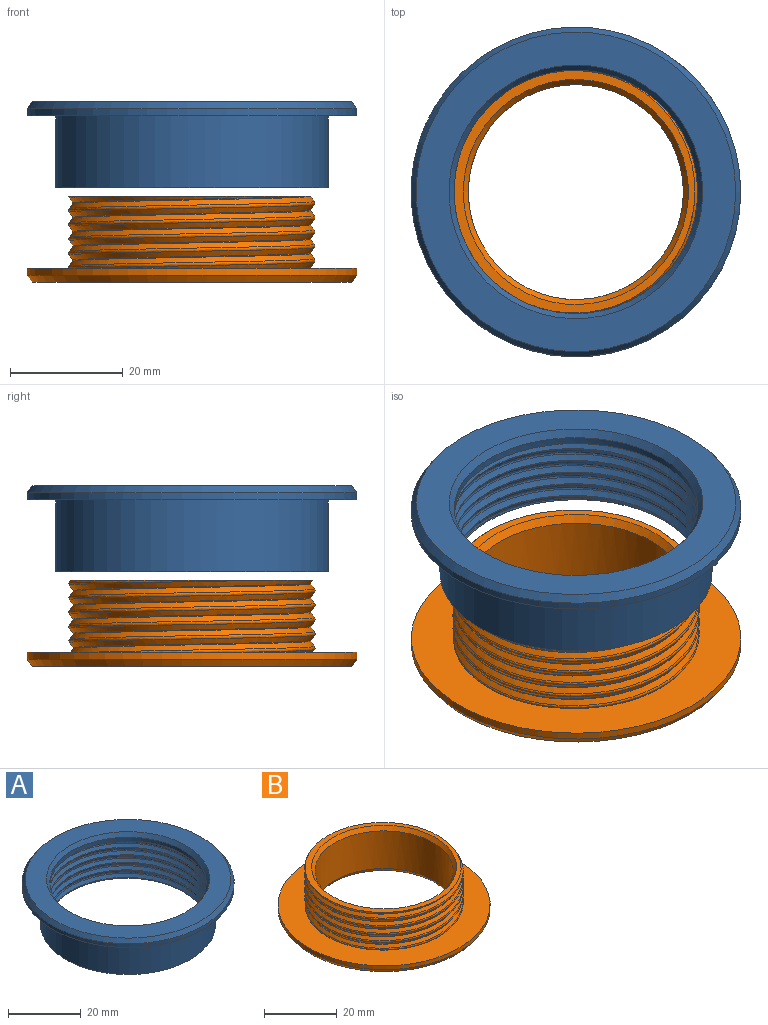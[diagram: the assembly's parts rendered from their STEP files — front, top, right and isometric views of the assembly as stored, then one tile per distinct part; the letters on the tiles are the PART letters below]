
ASSEMBLY  parts=2 mates=1
PART A: 17 faces, bbox 59.2x59.2x18.4 mm
  f0: cylinder r=24.13mm len=48.26mm, axis (0,0,-1), area 1925.5mm2, adj f1,f16
  f1: plane 58.42x58.42mm, normal (0,0,-1), area 851.3mm2, adj f0,f2
  f2: cylinder r=29.21mm len=58.42mm, axis (0,0,-1), area 233.1mm2, adj f1,f3
  f3: cone r=28.32mm half-angle=35deg, axis (0,0,-1), area 280.2mm2, adj f2,f4
  f4: plane 56.64x56.64mm, normal (0,0,1), area 932.3mm2, adj f3,f5
  f5: cone r=21.59mm half-angle=35deg, axis (0,0,1), area 214.6mm2, adj f4,f6
  f6: cylinder r=21.59mm len=43.18mm, axis (0,0,-1), area 189.1mm2, adj f5,f7,f13,f14,f15
  f7: bspline ~44.46x44.46mm, area 785.6mm2, adj f6,f8,f9,f11,f12,f13,f15,f16
  f8: bspline ~44.89x44.89mm, area 434.7mm2, adj f7,f14,f15,f16
  f9: cylinder r=21.59mm len=43.18mm, axis (0,0,-1), area 17.3mm2, adj f7,f10,f11,f14
  f10: cylinder r=21.59mm len=6.84mm, axis (0,0,-1), area 0.4mm2, adj f9,f14,f16
  f11: cylinder r=21.59mm len=43.18mm, axis (0,0,-1), area 17.3mm2, adj f7,f9,f12,f14
  f12: cylinder r=21.59mm len=43.18mm, axis (0,0,-1), area 17.3mm2, adj f7,f11,f13,f14
  f13: cylinder r=21.59mm len=43.18mm, axis (0,0,-1), area 17.3mm2, adj f6,f7,f12,f14
  f14: bspline ~45.54x45.48mm, area 201mm2, adj f6,f8,f9,f10,f11,f12,f13,f15
  f15: plane 44.77x44.7mm, normal (0,0,-1), area 53.9mm2, adj f6,f7,f8,f14
  f16: plane 48.71x48.71mm, normal (0,0,-1), area 311mm2, adj f0,f7,f8,f10,f14
PART B: 12 faces, bbox 58.9x58.9x17.1 mm
  f0: cylinder r=19.05mm len=38.1mm, axis (0,0,-1), area 1520.1mm2, adj f9,f11
  f1: cylinder r=21.08mm len=42.16mm, axis (0,0,-1), area 78mm2, adj f2,f3,f4,f6
  f2: bspline ~50.64x43.85mm, area 751.2mm2, adj f1,f4,f5,f6
  f3: bspline ~50.64x43.85mm, area 751.2mm2, adj f1,f4,f5,f6
  f4: plane 43.45x43.38mm, normal (0,0,1), area 199.9mm2, adj f1,f2,f3,f5,f11
  f5: bspline ~43.87x43.87mm, area 424.8mm2, adj f2,f3,f4,f6
  f6: plane 58.91x58.91mm, normal (0,0,1), area 1231.6mm2, adj f1,f2,f3,f5,f7
  f7: cylinder r=29.21mm len=58.42mm, axis (0,0,1), area 233.1mm2, adj f6,f10
  f8: plane 56.64x56.64mm, normal (0,0,-1), area 1270.7mm2, adj f9,f10
  f9: cone r=19.94mm half-angle=35deg, axis (0,0,-1), area 189.9mm2, adj f0,f8
  f10: cone r=29.21mm half-angle=35deg, axis (0,0,1), area 280.2mm2, adj f7,f8
  f11: cone r=19.94mm half-angle=35deg, axis (0,0,1), area 189.9mm2, adj f0,f4
PLACE A rot(axis=(0,0,-1),141.1deg) t=(1.14,12.37,32.17)mm
PLACE B t=(1.14,12.37,17.92)mm fixed
MATE cylindrical B.f0 <-> A.f0  axis (0,0,-1) through (1.14,12.37,16.65)mm
